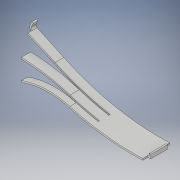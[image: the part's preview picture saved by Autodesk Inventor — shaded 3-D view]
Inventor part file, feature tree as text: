
AUTODESK INVENTOR PART (.ipt)
format: ipt  version: 2018.3 (Build 223284000, 284)  size: 212,480 bytes
history: native  units: in
note: dims shown in document units (in); Inventor stores cm internally (conversion verified against a paired STEP export)
features: extrude x6, sketch x4, plane x4
ambient origin geometry x8: Origin, YZ Plane, XZ Plane, XY Plane, X Axis, Y Axis, Z Axis, Center Point
bodies: Solid1 (feature_tree)
feature tree (14):
  sketch  "Sketch1"  dims[d3=9.0in d4=0.25in]
  extrude  "Extrusion1"  Depth=0.25in
  plane  "Work Plane6"
  extrude  "Extrusion2"  Depth=0.031in
  extrude  "Extrusion3"  Depth=0.015in
  plane  "Work Plane7"
  extrude  "Extrusion4"  Depth=0.532in TaperAngle=0.0deg
  plane  "Work Plane8"
  extrude  "Extrusion5"  Depth=0.185in TaperAngle=0.0deg
  plane  "Work Plane9"
  extrude  "Extrusion6"  Depth=0.122in
  sketch  "Sketch3"  dims[d5=0.031in d6=0.031in]
  sketch  "Sketch6"  dims[d7=0.078in d8=0.015in]
  sketch  "Sketch8"  dims[d14=1.06in d15=0.532in d16=0.0in d17=0.185in d18=0.0in d19=2.598in d20=0.384in d21=7.0in d28=0.135in d29=2.439in d30=3.0in d31=0.122in d32=0.0in d34=-0.147in d35=0.025in d42=0.66in d43=2.687in d44=0.031in d45=0.031in d46=0.155in d47=0.04in d50=0.0314in d51=0.175in d52=0.0in d53=0.0in d54=0.33in d55=0.165in d56=0.058in d57=0.058in d58=0.101in d59=0.122in d60=0.0in d61=0.0in d62=0.085in d63=0.122in d64=0.0in]
